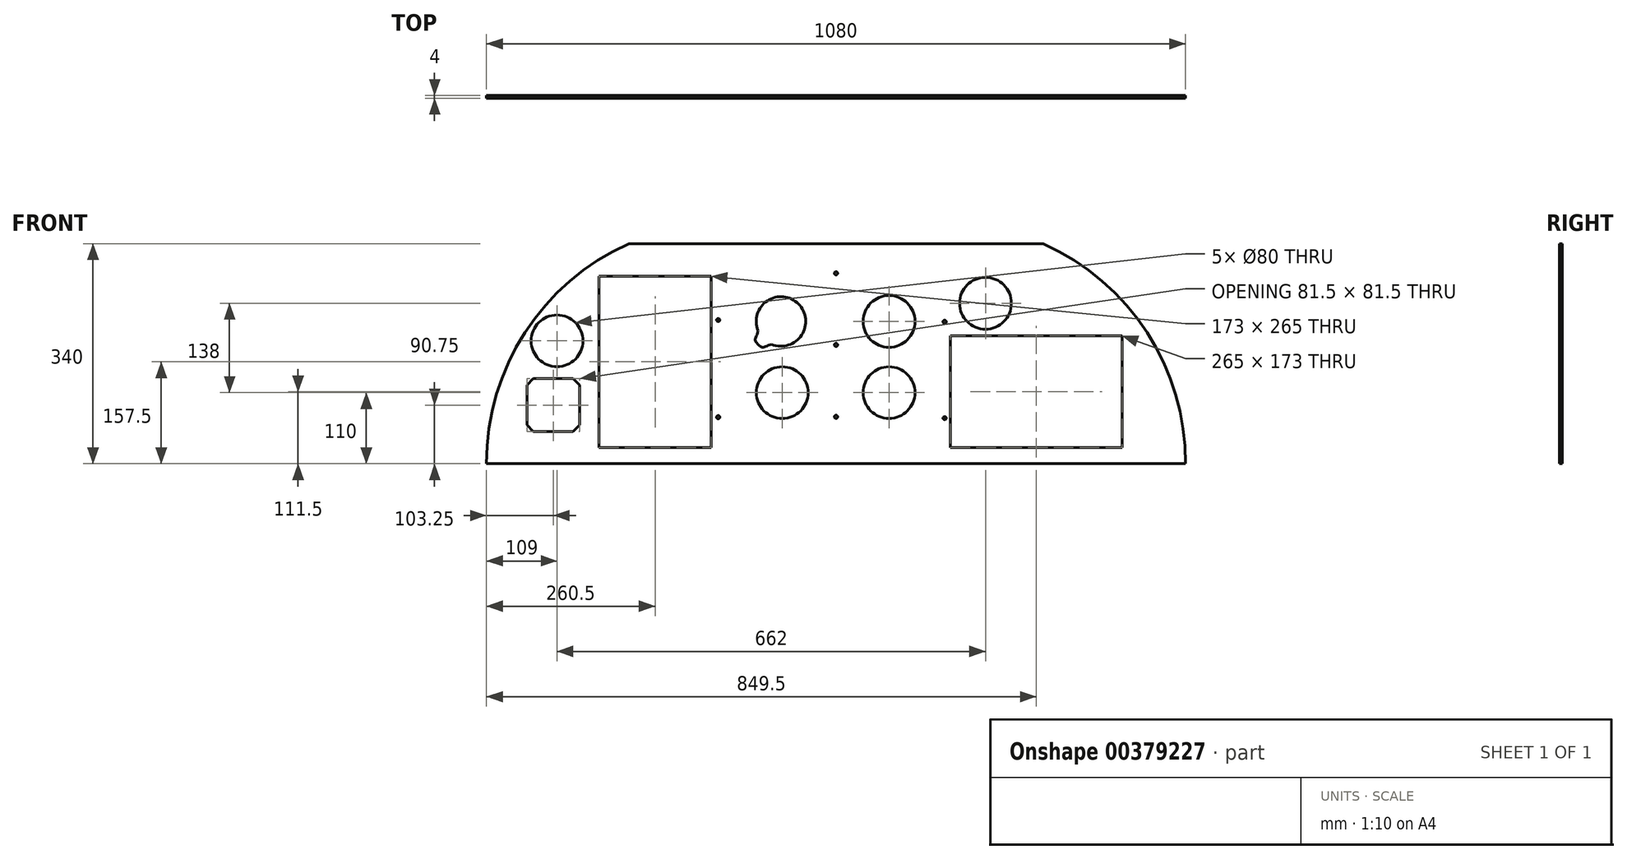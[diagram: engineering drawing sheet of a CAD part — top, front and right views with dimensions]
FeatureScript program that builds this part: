
annotation { "Feature Type Name" : "Feature", "Feature Type Description" : "" }
export const myFeature = defineFeature(function(context is Context, id is Id, definition is map)
    precondition{}
    {
        {
            var Q0;
            Q0=qCreatedBy(makeId("Front.planeOp"),FACE);
            var sketch = newSketch(context, id + "F0", { "sketchPlane" : qUnion([Q0])});
            skLineSegment(sketch, "E0", {"start": v(-540, -340) * mm, "end": v(540, -340) * mm});
            skLineSegment(sketch, "E1", {"start": v(-320, 0) * mm, "end": v(320, 0) * mm});
            skArc(sketch, "E2", {"start": v(-320, 0) * mm, "mid": v(-480.64, -137.23) * mm, "end": v(-540, -340) * mm});
            skArc(sketch, "E3", {"start": v(540, -340) * mm, "mid": v(480.64, -137.23) * mm, "end": v(320, 0) * mm});
            skSolve(sketch);
        }
        {
            var Q0;
            Q0=qSketchRegion(id+"F0",true);
            extrude(context, id + "F1", {"entities" : qUnion([Q0]), "depth" : 4 * mm});
        }
        {
            var Q0;
            Q0=makeQuery(id+"F1.opExtrude","CAP_FACE",FACE,{"disambiguationData":[OSD([sQuery(id+"F0.wireOp",EDGE,"E0"),sQuery(id+"F0.wireOp",EDGE,"E1"),sQuery(id+"F0.wireOp",EDGE,"E2"),sQuery(id+"F0.wireOp",EDGE,"E3")])],"isStart":false});
            var sketch = newSketch(context, id + "F2", { "sketchPlane" : qUnion([Q0])});
            skLineSegment(sketch, "E4", {"start": v(0, -340) * mm, "end": v(0, 0) * mm});
            skLineSegment(sketch, "E5", {"start": v(-9, -340) * mm, "end": v(0, -340) * mm});
            skLineSegment(sketch, "E6", {"start": v(0, -340) * mm, "end": v(9, -340) * mm});
            skLineSegment(sketch, "E7", {"start": v(0, -45) * mm, "end": v(-9, -45) * mm});
            skLineSegment(sketch, "E8", {"start": v(0, -45) * mm, "end": v(9, -45) * mm});
            skLineSegment(sketch, "E9", {"start": v(-9, -45) * mm, "end": v(-9, -340) * mm});
            skLineSegment(sketch, "E10", {"start": v(9, -45) * mm, "end": v(9, -340) * mm});
            skLineSegment(sketch, "E11", {"start": v(-191, -340) * mm, "end": v(-191, -80) * mm});
            skLineSegment(sketch, "E12", {"start": v(159, -340) * mm, "end": v(159, -120) * mm});
            skLineSegment(sketch, "E13", {"start": v(-191, -80) * mm, "end": v(-173, -80) * mm});
            skLineSegment(sketch, "E14", {"start": v(-173, -80) * mm, "end": v(-173, -340) * mm});
            skLineSegment(sketch, "E15", {"start": v(-191, -340) * mm, "end": v(-173, -340) * mm});
            skLineSegment(sketch, "E16", {"start": v(159, -120) * mm, "end": v(177, -120) * mm});
            skLineSegment(sketch, "E17", {"start": v(177, -120) * mm, "end": v(177, -340) * mm});
            skLineSegment(sketch, "E18", {"start": v(159, -340) * mm, "end": v(177, -340) * mm});
            skSolve(sketch);
        }
        {
            var Q0;
            {var subQ2=sQuery(id+"F2.wireOp",EDGE,"E8");Q0=makeQuery(id+"F2.imprint","IMPRINT",FACE,{"disambiguationData":[TD([[makeQuery(id+"F2.imprint","IMPRINT",EDGE,{"derivedFrom":subQ2}),1.0]])]});}
            var sketch = newSketch(context, id + "F3", { "sketchPlane" : qUnion([Q0])});
            skLineSegment(sketch, "E19.bottom", {"start": v(177, -142) * mm, "end": v(442, -142) * mm});
            skLineSegment(sketch, "E19.top", {"start": v(177, -315) * mm, "end": v(442, -315) * mm});
            skLineSegment(sketch, "E19.left", {"start": v(177, -142) * mm, "end": v(177, -315) * mm});
            skLineSegment(sketch, "E19.right", {"start": v(442, -142) * mm, "end": v(442, -315) * mm});
            skSolve(sketch);
        }
        {
            var Q0;
            Q0=makeQuery(id+"F3.imprint","IMPRINT",FACE,{"disambiguationData":[TD([[makeQuery(id+"F3.imprint","IMPRINT",EDGE,{"derivedFrom":sQuery(id+"F3.wireOp",EDGE,"E19.bottom")}),-1.0]])]});
            extrude(context, id + "F4", {"entities" : qUnion([Q0]), "operationType" : NewBodyOperationType.REMOVE, "oppositeDirection" : true, "depth" : 25 * mm});
        }
        {
            var Q0;
            Q0=qCreatedBy(makeId("Front.planeOp"),FACE);
            var sketch = newSketch(context, id + "F5", { "sketchPlane" : qUnion([Q0])});
            skLineSegment(sketch, "E20.bottom", {"start": v(-193, -315) * mm, "end": v(-366, -315) * mm});
            skLineSegment(sketch, "E20.top", {"start": v(-193, -50) * mm, "end": v(-366, -50) * mm});
            skLineSegment(sketch, "E20.left", {"start": v(-193, -315) * mm, "end": v(-193, -50) * mm});
            skLineSegment(sketch, "E20.right", {"start": v(-366, -315) * mm, "end": v(-366, -50) * mm});
            skSolve(sketch);
        }
        {
            var Q0;
            Q0=qSketchRegion(id+"F5",true);
            extrude(context, id + "F6", {"entities" : qUnion([Q0]), "operationType" : NewBodyOperationType.REMOVE, "depth" : 25 * mm});
        }
        {
            var Q0;
            Q0=qCreatedBy(makeId("Front.planeOp"),FACE);
            var sketch = newSketch(context, id + "F7", { "sketchPlane" : qUnion([Q0])});
            skCircle(sketch, "E21", {"center": v(-182.02, -268) * mm, "radius": 2.5 * mm});
            skCircle(sketch, "E22", {"center": v(-181.98, -117.82) * mm, "radius": 2.5 * mm});
            skCircle(sketch, "E23", {"center": v(0, -45.54) * mm, "radius": 2.5 * mm});
            skCircle(sketch, "E24", {"center": v(0, -156.32) * mm, "radius": 2.5 * mm});
            skCircle(sketch, "E25", {"center": v(0, -267.5) * mm, "radius": 2.5 * mm});
            skCircle(sketch, "E26", {"center": v(167.89, -120.6) * mm, "radius": 2.5 * mm});
            skCircle(sketch, "E27", {"center": v(167.89, -269.5) * mm, "radius": 2.5 * mm});
            skCircle(sketch, "E28", {"center": v(231, -92) * mm, "radius": 40 * mm});
            skCircle(sketch, "E29", {"center": v(82, -230) * mm, "radius": 40 * mm});
            skCircle(sketch, "E30", {"center": v(82, -120) * mm, "radius": 40 * mm});
            skCircle(sketch, "E31", {"center": v(-83, -230) * mm, "radius": 40 * mm});
            skCircle(sketch, "E32", {"center": v(-85, -120) * mm, "radius": 38.25 * mm});
            skSolve(sketch);
        }
        {
            var Q0;
            Q0=qSketchRegion(id+"F7",true);
            extrude(context, id + "F8", {"entities" : qUnion([Q0]), "operationType" : NewBodyOperationType.REMOVE, "oppositeDirection" : true, "depth" : 25 * mm});
        }
        {
            var Q0;
            Q0=qSketchRegion(id+"F7",true);
            extrude(context, id + "F9", {"entities" : qUnion([Q0]), "operationType" : NewBodyOperationType.REMOVE, "endBound" : BoundingType.SYMMETRIC, "oppositeDirection" : true, "depth" : 25 * mm});
        }
        {
            var Q0;
            {var subQ1=sQuery(id+"F2.wireOp",EDGE,"E7");Q0=makeQuery(id+"F2.imprint","IMPRINT",FACE,{"disambiguationData":[TD([[makeQuery(id+"F2.imprint","IMPRINT",EDGE,{"derivedFrom":subQ1}),-1.0]])]});}
            var sketch = newSketch(context, id + "F10", { "sketchPlane" : qUnion([Q0])});
            skLineSegment(sketch, "E33", {"start": v(-123.25, -120) * mm, "end": v(-46.75, -120) * mm, "construction": true});
            skPoint(sketch, "E34", {"position": v(-85, -120) * mm});
            skLineSegment(sketch, "E35", {"start": v(-85, -120) * mm, "end": v(-139.53, -174.53) * mm, "construction": true});
            skPoint(sketch, "E36", {"position": v(-120.49, -155.49) * mm});
            skLineSegment(sketch, "E37", {"start": v(-120.49, -134.27) * mm, "end": v(-99.27, -155.49) * mm, "construction": true});
            skPoint(sketch, "E38", {"position": v(-109.88, -144.88) * mm});
            skPoint(sketch, "E39", {"position": v(-125.08, -148.06) * mm});
            skPoint(sketch, "E40", {"position": v(-113.06, -160.08) * mm});
            skFitSpline(sketch, "E41", {"points": [v(-120.49, -134.27) * mm, v(-125.08, -148.06) * mm, v(-120.49, -155.49) * mm, v(-113.06, -160.08) * mm, v(-99.27, -155.49) * mm], "startDerivative": vector(-6.17, -77.7) * mm, "endDerivative": vector(68.34, 7.08) * mm});
            skLineSegment(sketch, "E42", {"start": v(-120.49, -134.27) * mm, "end": v(-99.27, -155.49) * mm});
            skSolve(sketch);
        }
        {
            var Q0;
            {var subQ2=sQuery(id+"F2.wireOp",EDGE,"E7");Q0=makeQuery(id+"F10.imprint","IMPRINT",FACE,{"disambiguationData":[TD([[makeQuery(id+"F10.imprint","IMPRINT",EDGE,{"derivedFrom":makeQuery(id+"F2.imprint","IMPRINT",EDGE,{"derivedFrom":subQ2})}),-1.0]])]});}
            var sketch = newSketch(context, id + "F11", { "sketchPlane" : qUnion([Q0])});
            skSolve(sketch);
        }
        {
            var Q0;
            Q0=makeQuery(id+"F10.imprint","IMPRINT",FACE,{"disambiguationData":[TD([[makeQuery(id+"F10.imprint","IMPRINT",EDGE,{"derivedFrom":sQuery(id+"F10.wireOp",EDGE,"E41")}),1.0]])]});
            extrude(context, id + "F12", {"entities" : qUnion([Q0]), "operationType" : NewBodyOperationType.REMOVE, "endBound" : BoundingType.THROUGH_ALL, "oppositeDirection" : true, "depth" : 25 * mm});
        }
        {
            var Q0;
            Q0=makeQuery(id+"F11.imprint","IMPRINT",FACE,{"disambiguationData":[TD([[makeQuery(id+"F11.imprint","IMPRINT",EDGE,{"derivedFrom":makeQuery(id+"F10.imprint","IMPRINT",EDGE,{"derivedFrom":sQuery(id+"F10.wireOp",EDGE,"E41")})}),-1.0]])]});
            var sketch = newSketch(context, id + "F13", { "sketchPlane" : qUnion([Q0])});
            skCircle(sketch, "E43", {"center": v(-431, -150) * mm, "radius": 40 * mm});
            skLineSegment(sketch, "E44", {"start": v(-396, -280) * mm, "end": v(-406, -290) * mm});
            skLineSegment(sketch, "E45", {"start": v(-477.5, -280) * mm, "end": v(-467.5, -290) * mm});
            skLineSegment(sketch, "E46", {"start": v(-467.5, -208.5) * mm, "end": v(-477.5, -218.5) * mm});
            skLineSegment(sketch, "E47", {"start": v(-406, -208.5) * mm, "end": v(-396, -218.5) * mm});
            skLineSegment(sketch, "E48", {"start": v(-406, -290) * mm, "end": v(-396, -280) * mm});
            skLineSegment(sketch, "E49", {"start": v(-396, -218.5) * mm, "end": v(-406, -208.5) * mm});
            skLineSegment(sketch, "E50", {"start": v(-467.5, -208.5) * mm, "end": v(-406, -208.5) * mm});
            skLineSegment(sketch, "E51", {"start": v(-477.5, -218.5) * mm, "end": v(-477.5, -280) * mm});
            skLineSegment(sketch, "E52", {"start": v(-467.5, -290) * mm, "end": v(-406, -290) * mm});
            skLineSegment(sketch, "E53", {"start": v(-396, -280) * mm, "end": v(-396, -218.5) * mm});
            skSolve(sketch);
        }
        {
            var Q0;
            Q0 = qSketchRegion(id + "F13", true);
            extrude(context, id + "F14", {"entities" : qUnion([Q0]), "operationType" : NewBodyOperationType.REMOVE, "oppositeDirection" : true, "depth" : 25 * mm});
        }
    });
